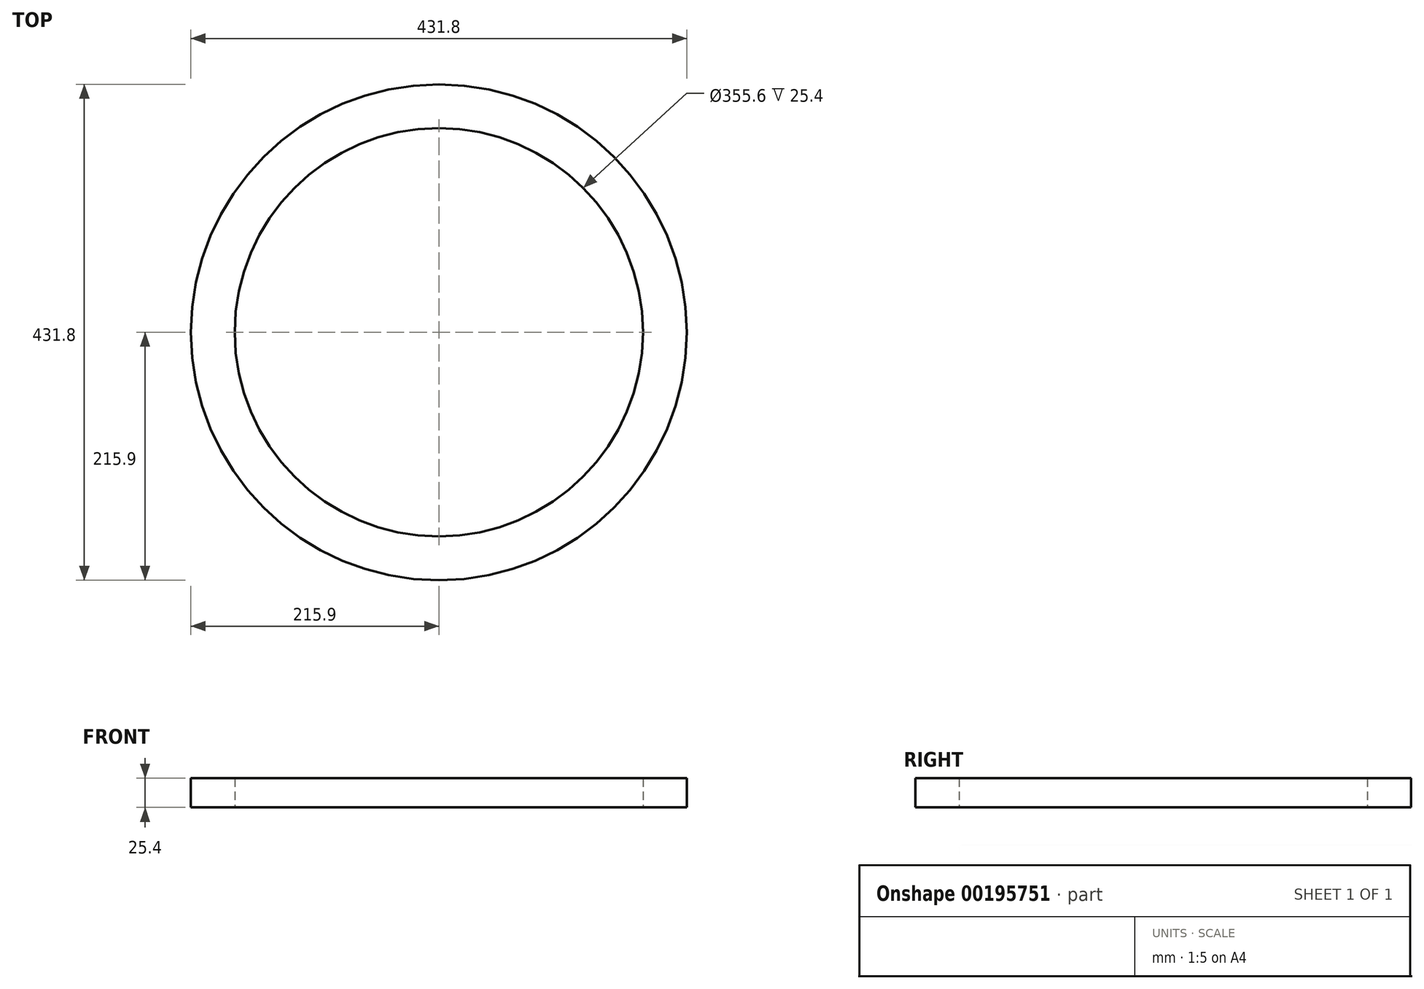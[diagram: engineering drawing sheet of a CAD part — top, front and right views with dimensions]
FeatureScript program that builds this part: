
annotation { "Feature Type Name" : "Feature", "Feature Type Description" : "" }
export const myFeature = defineFeature(function(context is Context, id is Id, definition is map)
    precondition{}
    {
        {
            var Q0;
            Q0=qCreatedBy(makeId("Top.planeOp"),FACE);
            var sketch = newSketch(context, id + "F0", { "sketchPlane" : qUnion([Q0])});
            skCircle(sketch, "E0", {"center": v(0, 0) * mm, "radius": 215.9 * mm});
            skCircle(sketch, "E1", {"center": v(0, 0) * mm, "radius": 177.8 * mm});
            skSolve(sketch);
        }
        {
            var Q0;
            Q0=qSketchRegion(id+"F0",true);
            extrude(context, id + "F1", {"entities" : qUnion([Q0]), "depth" : 25.4 * mm});
        }
        {
            var Q0;
            Q0=makeQuery(id+"F1.opExtrude","CAP_FACE",FACE,{"disambiguationData":[OSD([sQuery(id+"F0.wireOp",EDGE,"E0"),sQuery(id+"F0.wireOp",EDGE,"E1")])],"isStart":false});
            var sketch = newSketch(context, id + "F2", { "sketchPlane" : qUnion([Q0])});
            skCircle(sketch, "E2", {"center": v(29.21, 50.6) * mm, "radius": 5.08 * mm});
            skCircle(sketch, "E3.1.0", {"center": v(-29.2, 50.6) * mm, "radius": 5.08 * mm});
            skCircle(sketch, "E3.2.0", {"center": v(-58.42, 0) * mm, "radius": 5.08 * mm});
            skCircle(sketch, "E3.3.0", {"center": v(-29.21, -50.6) * mm, "radius": 5.08 * mm});
            skCircle(sketch, "E3.4.0", {"center": v(29.2, -50.6) * mm, "radius": 5.08 * mm});
            skCircle(sketch, "E3.5.0", {"center": v(58.42, 0) * mm, "radius": 5.08 * mm});
            skPoint(sketch, "E3.center", {"position": v(0, 0) * mm});
            skSolve(sketch);
        }
        {
            var Q0;
            Q0=qSketchRegion(id+"F2",true);
            extrude(context, id + "F3", {"entities" : qUnion([Q0]), "operationType" : NewBodyOperationType.REMOVE, "oppositeDirection" : true, "depth" : 38.1 * mm});
        }
    });
